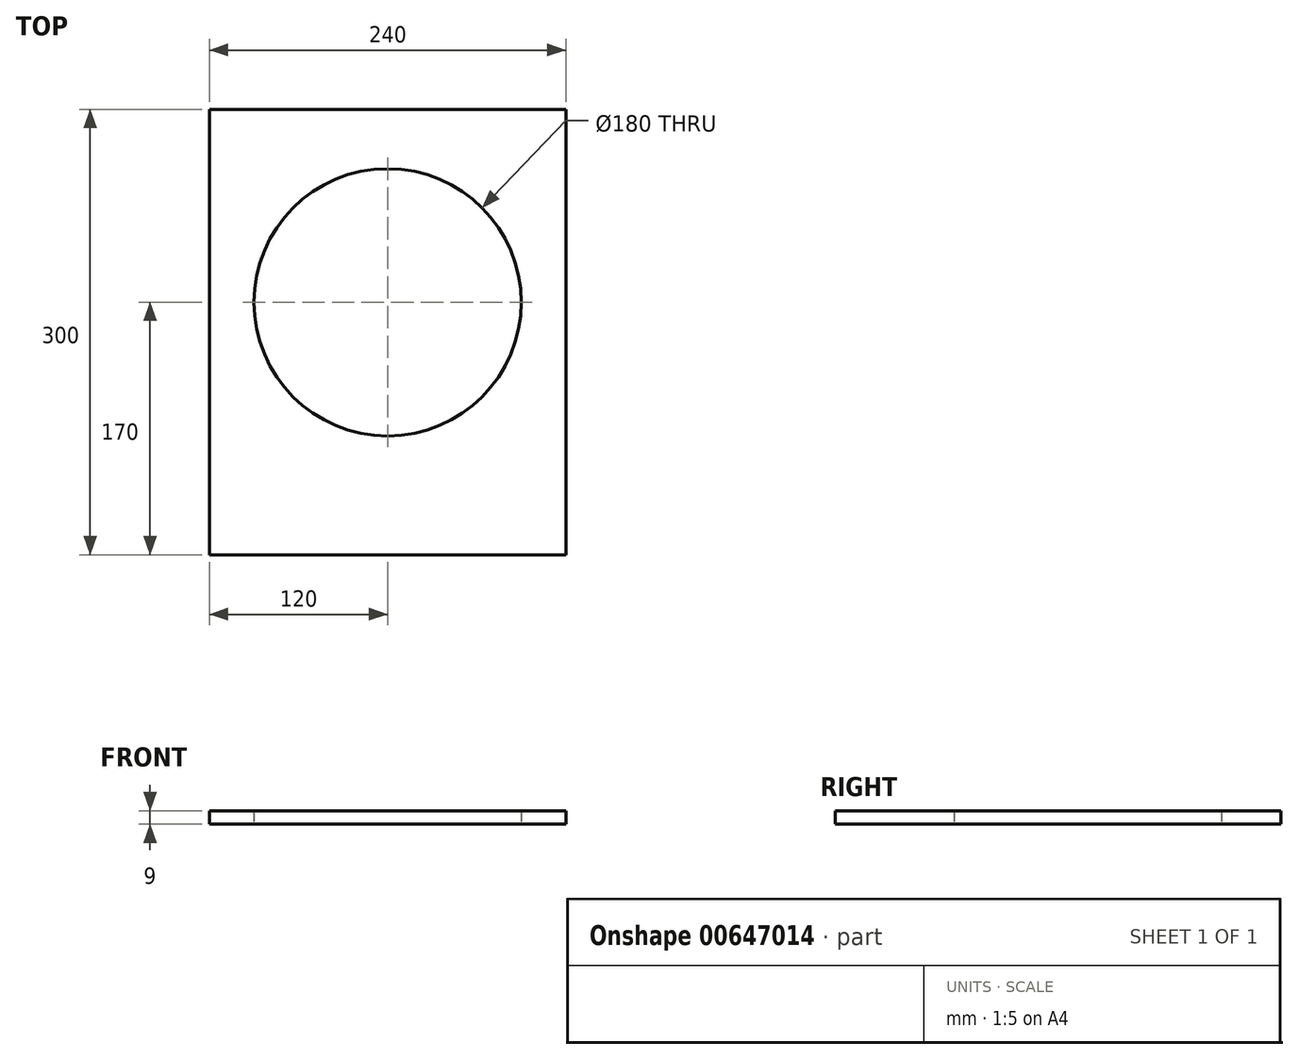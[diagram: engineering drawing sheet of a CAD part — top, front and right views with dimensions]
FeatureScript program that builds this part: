
annotation { "Feature Type Name" : "Feature", "Feature Type Description" : "" }
export const myFeature = defineFeature(function(context is Context, id is Id, definition is map)
    precondition{}
    {
        {
            var Q0;
            Q0=qCreatedBy(makeId("Top.planeOp"),FACE);
            var sketch = newSketch(context, id + "F0", { "sketchPlane" : qUnion([Q0])});
            skLineSegment(sketch, "E0.bottom", {"start": v(120, -150) * mm, "end": v(-120, -150) * mm});
            skLineSegment(sketch, "E0.top", {"start": v(120, 150) * mm, "end": v(-120, 150) * mm});
            skLineSegment(sketch, "E0.left", {"start": v(120, -150) * mm, "end": v(120, 150) * mm});
            skLineSegment(sketch, "E0.right", {"start": v(-120, -150) * mm, "end": v(-120, 150) * mm});
            skPoint(sketch, "E0.middle", {"position": v(0, 0) * mm});
            skCircle(sketch, "E1", {"center": v(0, 20) * mm, "radius": 90 * mm});
            skSolve(sketch);
        }
        {
            var Q0;
            Q0 = qSketchRegion(id + "F0", true);
            extrude(context, id + "F1", {"entities" : qUnion([Q0]), "depth" : 9 * mm, "offsetDistance" : 25 * mm});
        }
    });
